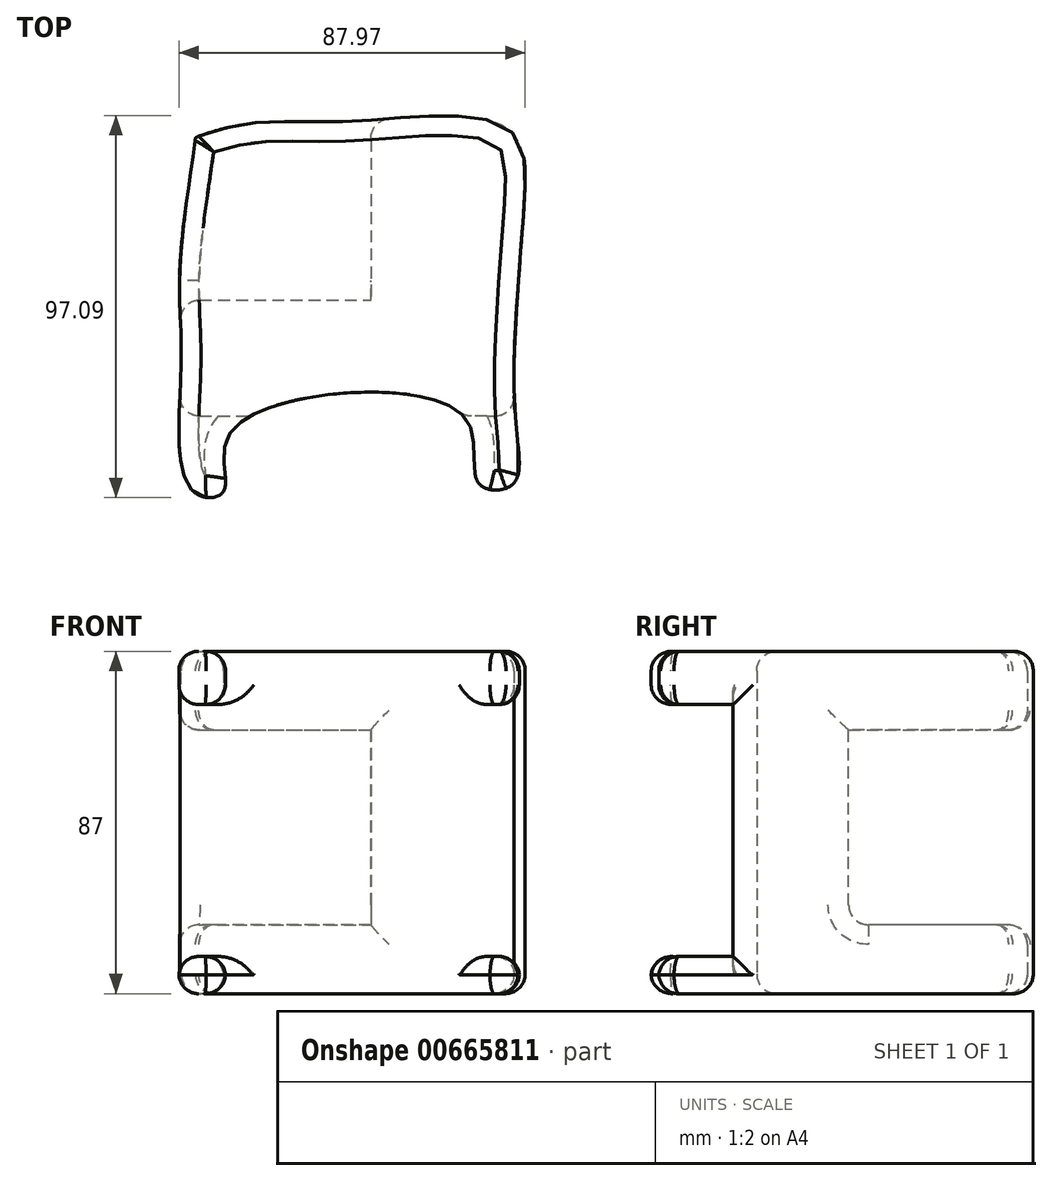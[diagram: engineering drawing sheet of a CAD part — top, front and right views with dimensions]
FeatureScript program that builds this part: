
annotation { "Feature Type Name" : "Feature", "Feature Type Description" : "" }
export const myFeature = defineFeature(function(context is Context, id is Id, definition is map)
    precondition{}
    {
        {
            var Q0;
            Q0=qCreatedBy(makeId("Top.planeOp"),FACE);
            var sketch = newSketch(context, id + "F0", { "sketchPlane" : qUnion([Q0])});
            skFitSpline(sketch, "E0", {"points": [v(-36.23, 43.92) * mm, v(-44.42, 41.32) * mm, v(-44.62, 40.72) * mm, v(-48.4, 10.58) * mm, v(-48.2, -16.77) * mm, v(-45.41, -48.3) * mm, v(-37.43, -48.5) * mm, v(-35.23, -32.94) * mm, v(22.86, -28.75) * mm, v(27.25, -46.31) * mm, v(35.83, -46.91) * mm, v(36.63, -29.14) * mm, v(38.83, 22.76) * mm, v(36.03, 42.52) * mm, v(19.46, 46.91) * mm, v(-4.7, 45.51) * mm, v(-27.25, 45.31) * mm, v(-36.23, 43.92) * mm]});
            skSolve(sketch);
        }
        {
            var Q0;
            Q0 = qSketchRegion(id + "F0", true);
            extrude(context, id + "F1", {"entities" : qUnion([Q0]), "depth" : 87 * mm, "offsetDistance" : 25 * mm});
        }
        {
            var Q0;
            Q0=qCreatedBy(makeId("Right.planeOp"),FACE);
            var sketch = newSketch(context, id + "F2", { "sketchPlane" : qUnion([Q0])});
            skLineSegment(sketch, "E1.bottom", {"start": v(-54.87, 73.48) * mm, "end": v(-29.43, 73.48) * mm});
            skLineSegment(sketch, "E1.top", {"start": v(-54.87, 9.45) * mm, "end": v(-29.43, 9.45) * mm});
            skLineSegment(sketch, "E1.left", {"start": v(-54.87, 73.48) * mm, "end": v(-54.87, 9.45) * mm});
            skLineSegment(sketch, "E1.right", {"start": v(-29.43, 73.48) * mm, "end": v(-29.43, 9.45) * mm});
            skSolve(sketch);
        }
        {
            var Q0;
            Q0 = qSketchRegion(id + "F2", true);
            extrude(context, id + "F3", {"entities" : qUnion([Q0]), "operationType" : NewBodyOperationType.REMOVE, "oppositeDirection" : true, "depth" : 53.1 * mm, "offsetDistance" : 25 * mm, "hasSecondDirection" : true, "secondDirectionOppositeDirection" : false, "secondDirectionDepth" : 86.7 * mm});
        }
        {
            var Q0;
            Q0=qCreatedBy(makeId("Right.planeOp"),FACE);
            var sketch = newSketch(context, id + "F4", { "sketchPlane" : qUnion([Q0])});
            skLineSegment(sketch, "E2.bottom", {"start": v(48.82, 17.51) * mm, "end": v(0, 17.51) * mm});
            skLineSegment(sketch, "E2.top", {"start": v(48.82, 67) * mm, "end": v(0, 67) * mm});
            skLineSegment(sketch, "E2.left", {"start": v(48.82, 17.51) * mm, "end": v(48.82, 67) * mm});
            skLineSegment(sketch, "E2.right", {"start": v(0, 17.51) * mm, "end": v(0, 67) * mm});
            skSolve(sketch);
        }
        {
            var Q0;
            Q0 = qSketchRegion(id + "F4", true);
            extrude(context, id + "F5", {"entities" : qUnion([Q0]), "operationType" : NewBodyOperationType.REMOVE, "oppositeDirection" : true, "depth" : 70 * mm, "offsetDistance" : 25 * mm});
        }
        {
            var Q0;
            Q0=makeQuery(id+"F5.boolean.opBoolean","INTERSECT",EDGE,{"derivedFrom":[makeQuery(id+"F1.opExtrude","SWEPT_FACE",FACE,{"disambiguationData":[OSD([sQuery(id+"F0.wireOp",EDGE,"E0")])]}),makeQuery(id+"F5.opExtrude","CAP_FACE",FACE,{"disambiguationData":[OSD([sQuery(id+"F4.wireOp",EDGE,"E2.bottom"),sQuery(id+"F4.wireOp",EDGE,"E2.top"),sQuery(id+"F4.wireOp",EDGE,"E2.left"),sQuery(id+"F4.wireOp",EDGE,"E2.right")])],"isStart":true})]});
            var Q1;
            Q1=makeQuery(id+"F1.opExtrude","CAP_EDGE",EDGE,{"disambiguationData":[OSD([sQuery(id+"F0.wireOp",EDGE,"E0")])],"isStart":false});
            var Q2;
            Q2=makeQuery(id+"F1.opExtrude","CAP_EDGE",EDGE,{"disambiguationData":[OSD([sQuery(id+"F0.wireOp",EDGE,"E0")])],"isStart":true});
            var Q3;
            Q3=makeQuery(id+"F1.opExtrude","SWEPT_FACE",FACE,{"disambiguationData":[OSD([sQuery(id+"F0.wireOp",EDGE,"E0")])]});
            var Q4;
            Q4=makeQuery(id+"F5.boolean.opBoolean","INTERSECT",EDGE,{"derivedFrom":[makeQuery(id+"F1.opExtrude","SWEPT_FACE",FACE,{"disambiguationData":[OSD([sQuery(id+"F0.wireOp",EDGE,"E0")])]}),makeQuery(id+"F5.opExtrude","SWEPT_FACE",FACE,{"disambiguationData":[OSD([sQuery(id+"F4.wireOp",EDGE,"E2.right")])]})]});
            var Q5;
            Q5=makeQuery(id+"F5.boolean.opBoolean","INTERSECT",EDGE,{"derivedFrom":[makeQuery(id+"F1.opExtrude","SWEPT_FACE",FACE,{"disambiguationData":[OSD([sQuery(id+"F0.wireOp",EDGE,"E0")])]}),makeQuery(id+"F5.opExtrude","SWEPT_FACE",FACE,{"disambiguationData":[OSD([sQuery(id+"F4.wireOp",EDGE,"E2.top")])]})]});
            var Q6;
            Q6=makeQuery(id+"F5.boolean.opBoolean","COPY",EDGE,{"derivedFrom":makeQuery(id+"F5.opExtrude","SWEPT_EDGE",EDGE,{"disambiguationData":[OSD([sQuery(id+"F4.wireOp",EDGE,"E2.bottom"),sQuery(id+"F4.wireOp",EDGE,"E2.right")])]})});
            var Q7;
            Q7=makeQuery(id+"F5.boolean.opBoolean","INTERSECT",EDGE,{"derivedFrom":[makeQuery(id+"F1.opExtrude","SWEPT_FACE",FACE,{"disambiguationData":[OSD([sQuery(id+"F0.wireOp",EDGE,"E0")])]}),makeQuery(id+"F5.opExtrude","SWEPT_FACE",FACE,{"disambiguationData":[OSD([sQuery(id+"F4.wireOp",EDGE,"E2.bottom")])]})]});
            fillet(context, id + "F6", {"entities" : qUnion([Q0, Q1, Q2, Q3, Q4, Q5, Q6, Q7]), "radius" : 5 * mm, "tangentPropagation" : true, "allowEdgeOverflow" : false});
        }
    });
